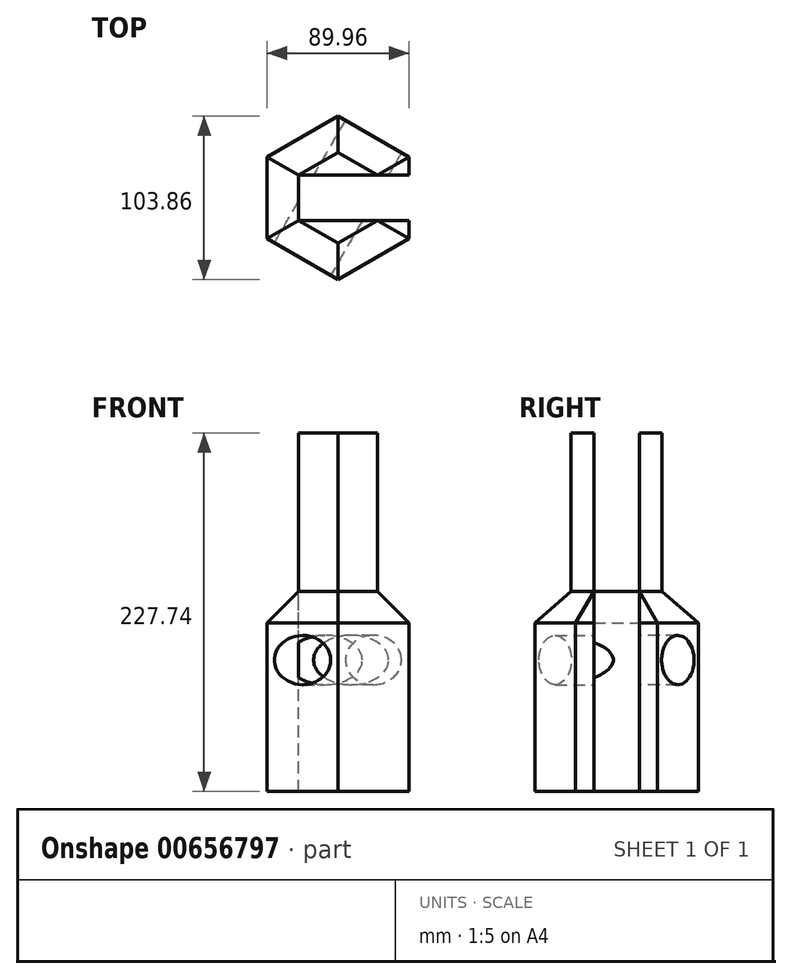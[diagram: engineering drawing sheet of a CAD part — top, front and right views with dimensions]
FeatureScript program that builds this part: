
annotation { "Feature Type Name" : "Feature", "Feature Type Description" : "" }
export const myFeature = defineFeature(function(context is Context, id is Id, definition is map)
    precondition{}
    {
        {
            var Q0;
            Q0=qCreatedBy(makeId("Top.planeOp"),FACE);
            var sketch = newSketch(context, id + "F0", { "sketchPlane" : qUnion([Q0])});
            skCircle(sketch, "E0.cCircle", {"center": v(0, 0) * mm, "radius": 51.93 * mm, "construction": true});
            skLineSegment(sketch, "E0.0", {"start": v(0, -51.93) * mm, "end": v(-44.98, -25.97) * mm});
            skLineSegment(sketch, "E0.1", {"start": v(-44.98, -25.97) * mm, "end": v(-44.98, 25.97) * mm});
            skLineSegment(sketch, "E0.2", {"start": v(-44.98, 25.97) * mm, "end": v(0, 51.93) * mm});
            skLineSegment(sketch, "E0.3", {"start": v(0, 51.93) * mm, "end": v(44.98, 25.97) * mm});
            skLineSegment(sketch, "E0.4", {"start": v(44.98, 25.97) * mm, "end": v(44.98, -25.97) * mm});
            skLineSegment(sketch, "E0.5", {"start": v(44.98, -25.97) * mm, "end": v(0, -51.93) * mm});
            skSolve(sketch);
        }
        {
            var Q0;
            Q0 = qSketchRegion(id + "F0", true);
            extrude(context, id + "F1", {"entities" : qUnion([Q0]), "depth" : 127 * mm, "offsetDistance" : 25.4 * mm});
        }
        {
            var Q0;
            Q0=makeQuery(id+"F1.opExtrude","CAP_EDGE",EDGE,{"disambiguationData":[OSD([sQuery(id+"F0.wireOp",EDGE,"E0.1")])],"isStart":false});
            var Q1;
            Q1=makeQuery(id+"F1.opExtrude","CAP_EDGE",EDGE,{"disambiguationData":[OSD([sQuery(id+"F0.wireOp",EDGE,"E0.2")])],"isStart":false});
            var Q2;
            Q2=makeQuery(id+"F1.opExtrude","CAP_EDGE",EDGE,{"disambiguationData":[OSD([sQuery(id+"F0.wireOp",EDGE,"E0.3")])],"isStart":false});
            var Q3;
            Q3=makeQuery(id+"F1.opExtrude","CAP_EDGE",EDGE,{"disambiguationData":[OSD([sQuery(id+"F0.wireOp",EDGE,"E0.4")])],"isStart":false});
            var Q4;
            Q4=makeQuery(id+"F1.opExtrude","CAP_EDGE",EDGE,{"disambiguationData":[OSD([sQuery(id+"F0.wireOp",EDGE,"E0.5")])],"isStart":false});
            var Q5;
            Q5=makeQuery(id+"F1.opExtrude","CAP_EDGE",EDGE,{"disambiguationData":[OSD([sQuery(id+"F0.wireOp",EDGE,"E0.0")])],"isStart":false});
            chamfer(context, id + "F2", {"entities" : qUnion([Q0, Q1, Q2, Q3, Q4, Q5]), "width" : 20 * mm, "tangentPropagation" : true});
        }
        {
            var Q0;
            Q0=makeQuery(id+"F1.opExtrude","CAP_FACE",FACE,{"disambiguationData":[OSD([sQuery(id+"F0.wireOp",EDGE,"E0.0"),sQuery(id+"F0.wireOp",EDGE,"E0.1"),sQuery(id+"F0.wireOp",EDGE,"E0.2"),sQuery(id+"F0.wireOp",EDGE,"E0.3"),sQuery(id+"F0.wireOp",EDGE,"E0.4"),sQuery(id+"F0.wireOp",EDGE,"E0.5")])],"isStart":false});
            extrude(context, id + "F3", {"entities" : qUnion([Q0]), "operationType" : NewBodyOperationType.ADD, "depth" : 100.74 * mm, "offsetDistance" : 25 * mm});
        }
        {
            var Q0;
            Q0=makeQuery(id+"F3.opExtrude","CAP_FACE",FACE,{"disambiguationData":[OSD([sQuery(id+"F0.wireOp",EDGE,"E0.0"),sQuery(id+"F0.wireOp",EDGE,"E0.1"),sQuery(id+"F0.wireOp",EDGE,"E0.2"),sQuery(id+"F0.wireOp",EDGE,"E0.3"),sQuery(id+"F0.wireOp",EDGE,"E0.4"),sQuery(id+"F0.wireOp",EDGE,"E0.5")])],"isStart":false});
            var sketch = newSketch(context, id + "F4", { "sketchPlane" : qUnion([Q0])});
            skLineSegment(sketch, "E1.bottom", {"start": v(-24.98, 14.42) * mm, "end": v(48.95, 14.42) * mm});
            skLineSegment(sketch, "E1.top", {"start": v(-24.98, -14.42) * mm, "end": v(48.95, -14.42) * mm});
            skLineSegment(sketch, "E1.left", {"start": v(-24.98, 14.42) * mm, "end": v(-24.98, -14.42) * mm});
            skLineSegment(sketch, "E1.right", {"start": v(48.95, 14.42) * mm, "end": v(48.95, -14.42) * mm});
            skSolve(sketch);
        }
        {
            var Q0;
            Q0 = qSketchRegion(id + "F4", true);
            extrude(context, id + "F5", {"entities" : qUnion([Q0]), "operationType" : NewBodyOperationType.REMOVE, "endBound" : BoundingType.THROUGH_ALL, "oppositeDirection" : true, "depth" : 25 * mm, "offsetDistance" : 25 * mm});
        }
        {
            var Q0;
            Q0=makeQuery(id+"F1.opExtrude","SWEPT_FACE",FACE,{"disambiguationData":[OSD([sQuery(id+"F0.wireOp",EDGE,"E0.5")])]});
            var sketch = newSketch(context, id + "F6", { "sketchPlane" : qUnion([Q0])});
            skEllipse(sketch, "E2", {"center": v(0, 86.66) * mm, "majorRadius": 15.43 * mm, "minorRadius": 43.98 * mm, "majorAxis": v(1, 0)});
            skSolve(sketch);
        }
        {
            var Q0;
            Q0=sQuery(id+"F6.wireOp",EDGE,"E2");
            extrude(context, id + "F7", {"bodyType" : ToolBodyType.SURFACE, "surfaceEntities" : qUnion([Q0]), "depth" : 25 * mm, "offsetDistance" : 25 * mm});
        }
        {
            var Q0;
            Q0=makeQuery(id+"F1.opExtrude","SWEPT_FACE",FACE,{"disambiguationData":[OSD([sQuery(id+"F0.wireOp",EDGE,"E0.0")])]});
            var sketch = newSketch(context, id + "F8", { "sketchPlane" : qUnion([Q0])});
            skEllipse(sketch, "E3", {"center": v(0, 83.54) * mm, "majorRadius": 15.68 * mm, "minorRadius": 20.62 * mm, "majorAxis": v(0, -1)});
            skSolve(sketch);
        }
        {
            var Q0;
            Q0=makeQuery(id+"F1.opExtrude","SWEPT_FACE",FACE,{"disambiguationData":[OSD([sQuery(id+"F0.wireOp",EDGE,"E0.2")])]});
            var sketch = newSketch(context, id + "F9", { "sketchPlane" : qUnion([Q0])});
            skEllipse(sketch, "E4", {"center": v(6.34, 63.34) * mm, "majorRadius": 15.3 * mm, "minorRadius": 5.94 * mm, "majorAxis": v(0, -1)});
            skSolve(sketch);
        }
        {
            var Q0;
            Q0=makeQuery(id+"F8.imprint","IMPRINT",FACE,{"disambiguationData":[TD([[makeQuery(id+"F8.imprint","IMPRINT",EDGE,{"derivedFrom":sQuery(id+"F8.wireOp",EDGE,"E3")}),1.0]])]});
            var Q1;
            Q1=sQuery(id+"F9.wireOp",EDGE,"E4");
            extrude(context, id + "F10", {"entities" : qUnion([Q0]), "operationType" : NewBodyOperationType.REMOVE, "surfaceEntities" : qUnion([Q1]), "endBound" : BoundingType.THROUGH_ALL, "oppositeDirection" : true, "depth" : 25 * mm, "offsetDistance" : 25 * mm});
        }
    });
